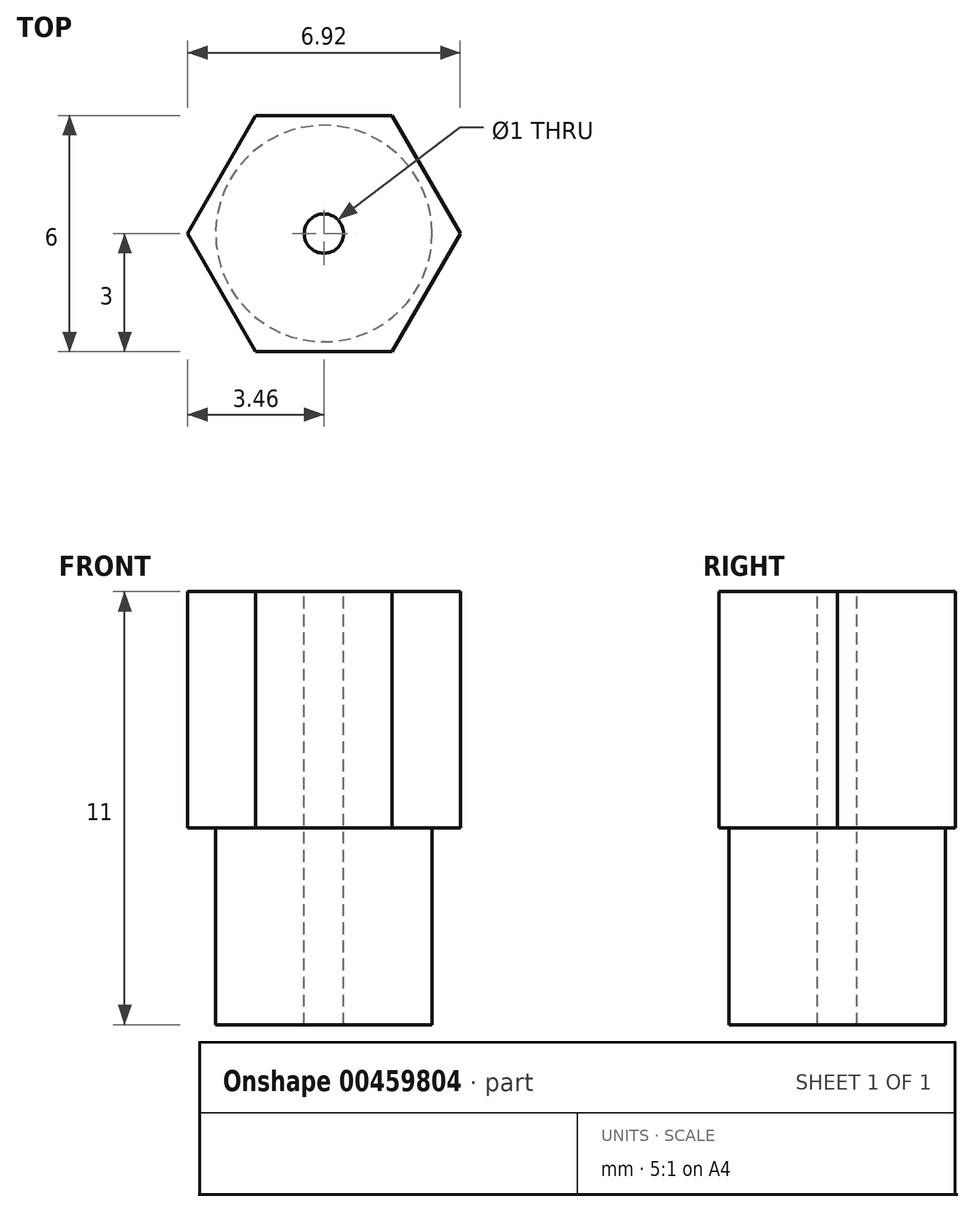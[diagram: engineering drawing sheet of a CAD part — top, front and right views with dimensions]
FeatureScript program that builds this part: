
annotation { "Feature Type Name" : "Feature", "Feature Type Description" : "" }
export const myFeature = defineFeature(function(context is Context, id is Id, definition is map)
    precondition{}
    {
        {
            var Q0;
            Q0=qCreatedBy(makeId("Top.planeOp"),FACE);
            var sketch = newSketch(context, id + "F0", { "sketchPlane" : qUnion([Q0])});
            skCircle(sketch, "E0", {"center": v(0, 0) * mm, "radius": 2.75 * mm});
            skSolve(sketch);
        }
        {
            var Q0;
            Q0 = qSketchRegion(id + "F0", true);
            extrude(context, id + "F1", {"entities" : qUnion([Q0]), "oppositeDirection" : true, "depth" : 5 * mm});
        }
        {
            var Q0;
            Q0=qCreatedBy(makeId("Top.planeOp"),FACE);
            var sketch = newSketch(context, id + "F2", { "sketchPlane" : qUnion([Q0])});
            skCircle(sketch, "E1.cCircle", {"center": v(0, 0) * mm, "radius": 3 * mm, "construction": true});
            skLineSegment(sketch, "E1.0", {"start": v(3.46, 0) * mm, "end": v(1.73, -3) * mm});
            skLineSegment(sketch, "E1.1", {"start": v(1.73, -3) * mm, "end": v(-1.73, -3) * mm});
            skLineSegment(sketch, "E1.2", {"start": v(-1.73, -3) * mm, "end": v(-3.46, 0) * mm});
            skLineSegment(sketch, "E1.3", {"start": v(-3.46, 0) * mm, "end": v(-1.73, 3) * mm});
            skLineSegment(sketch, "E1.4", {"start": v(-1.73, 3) * mm, "end": v(1.73, 3) * mm});
            skLineSegment(sketch, "E1.5", {"start": v(1.73, 3) * mm, "end": v(3.46, 0) * mm});
            skPoint(sketch, "E1.0.midPoint", {"position": v(2.6, -1.5) * mm});
            skSolve(sketch);
        }
        {
            var Q0;
            Q0 = qSketchRegion(id + "F2", true);
            extrude(context, id + "F3", {"entities" : qUnion([Q0]), "operationType" : NewBodyOperationType.ADD, "depth" : 6 * mm});
        }
        {
            var Q0;
            Q0=makeQuery(id+"F3.opExtrude","CAP_FACE",FACE,{"disambiguationData":[OSD([sQuery(id+"F2.wireOp",EDGE,"E1.0"),sQuery(id+"F2.wireOp",EDGE,"E1.1"),sQuery(id+"F2.wireOp",EDGE,"E1.2"),sQuery(id+"F2.wireOp",EDGE,"E1.3"),sQuery(id+"F2.wireOp",EDGE,"E1.4"),sQuery(id+"F2.wireOp",EDGE,"E1.5")])],"isStart":false});
            var sketch = newSketch(context, id + "F4", { "sketchPlane" : qUnion([Q0])});
            skCircle(sketch, "E2", {"center": v(0, 0) * mm, "radius": 0.5 * mm});
            skSolve(sketch);
        }
        {
            var Q0;
            Q0=makeQuery(id+"F4.imprint","IMPRINT",FACE,{"disambiguationData":[TD([[makeQuery(id+"F4.imprint","IMPRINT",EDGE,{"derivedFrom":sQuery(id+"F4.wireOp",EDGE,"E2")}),1.0]])]});
            extrude(context, id + "F5", {"entities" : qUnion([Q0]), "operationType" : NewBodyOperationType.REMOVE, "endBound" : BoundingType.THROUGH_ALL, "oppositeDirection" : true, "depth" : 25 * mm});
        }
    });
